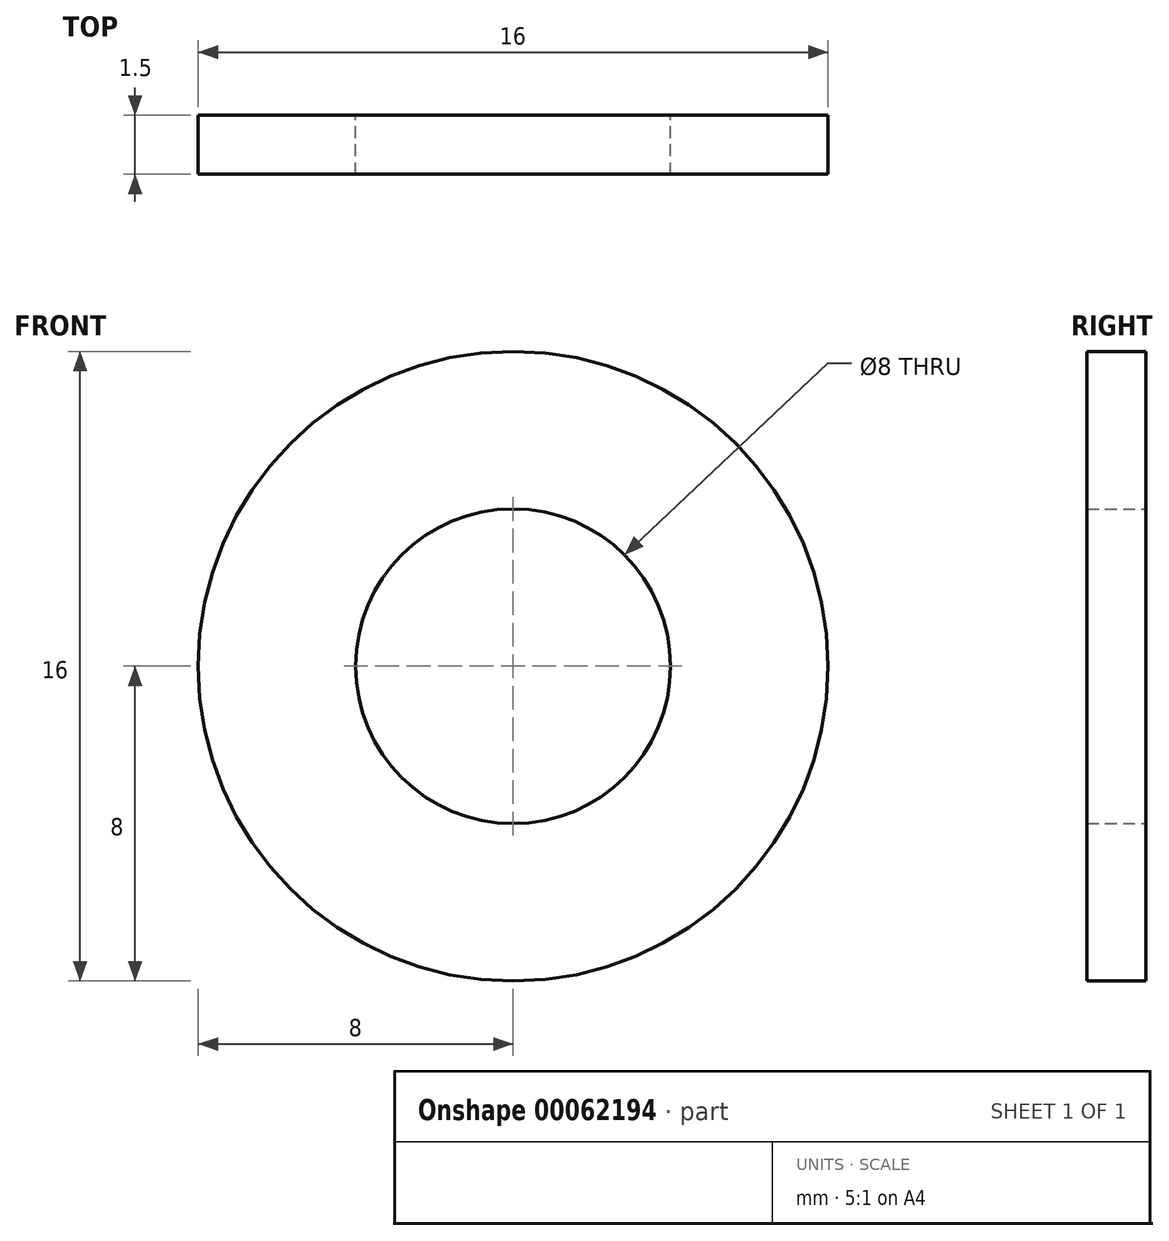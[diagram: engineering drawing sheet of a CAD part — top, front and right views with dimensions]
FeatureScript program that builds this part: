
annotation { "Feature Type Name" : "Feature", "Feature Type Description" : "" }
export const myFeature = defineFeature(function(context is Context, id is Id, definition is map)
    precondition{}
    {
        {
            var Q0;
            Q0=qCreatedBy(makeId("Front.planeOp"),FACE);
            var sketch = newSketch(context, id + "F0", { "sketchPlane" : qUnion([Q0])});
            skCircle(sketch, "E0", {"center": v(0, 0) * mm, "radius": 4 * mm});
            skCircle(sketch, "E1", {"center": v(0, 0) * mm, "radius": 8 * mm});
            skSolve(sketch);
        }
        {
            var Q0;
            Q0 = qSketchRegion(id + "F0", true);
            extrude(context, id + "F1", {"entities" : qUnion([Q0]), "depth" : 1.5 * mm});
        }
    });
